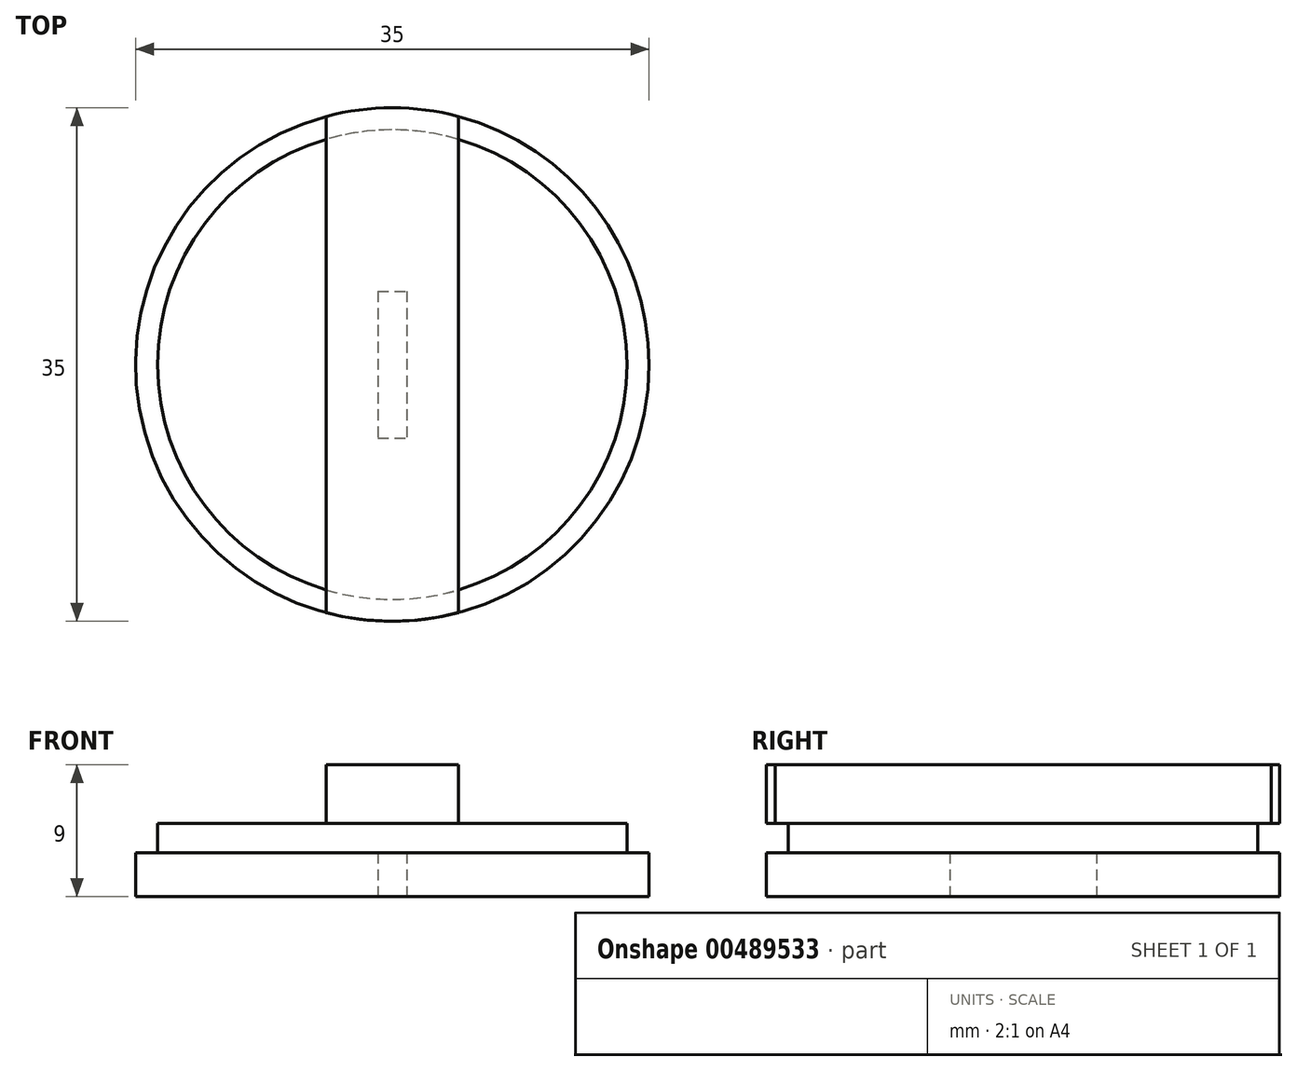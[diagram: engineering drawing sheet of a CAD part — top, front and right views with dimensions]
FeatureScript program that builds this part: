
annotation { "Feature Type Name" : "Feature", "Feature Type Description" : "" }
export const myFeature = defineFeature(function(context is Context, id is Id, definition is map)
    precondition{}
    {
        {
            var Q0;
            Q0=qCreatedBy(makeId("Top.planeOp"),FACE);
            var sketch = newSketch(context, id + "F0", { "sketchPlane" : qUnion([Q0])});
            skCircle(sketch, "E0", {"center": v(0, 0) * mm, "radius": 17.5 * mm});
            skSolve(sketch);
        }
        {
            var Q0;
            Q0 = qSketchRegion(id + "F0", true);
            extrude(context, id + "F1", {"entities" : qUnion([Q0]), "depth" : 3 * mm});
        }
        {
            var Q0;
            Q0=makeQuery(id+"F1.opExtrude","CAP_FACE",FACE,{"disambiguationData":[OSD([sQuery(id+"F0.wireOp",EDGE,"E0")])],"isStart":false});
            var sketch = newSketch(context, id + "F2", { "sketchPlane" : qUnion([Q0])});
            skCircle(sketch, "E1", {"center": v(0, 0) * mm, "radius": 16 * mm});
            skSolve(sketch);
        }
        {
            var Q0;
            Q0 = qSketchRegion(id + "F2", true);
            extrude(context, id + "F3", {"entities" : qUnion([Q0]), "operationType" : NewBodyOperationType.ADD, "depth" : 2 * mm});
        }
        {
            var Q0;
            Q0=makeQuery(id+"F3.opExtrude","CAP_FACE",FACE,{"disambiguationData":[OSD([sQuery(id+"F2.wireOp",EDGE,"E1")])],"isStart":false});
            var sketch = newSketch(context, id + "F4", { "sketchPlane" : qUnion([Q0])});
            skLineSegment(sketch, "E2.left", {"start": v(4.5, 16.91) * mm, "end": v(4.5, -16.91) * mm});
            skLineSegment(sketch, "E2.right", {"start": v(-4.5, 16.91) * mm, "end": v(-4.5, -16.91) * mm});
            skPoint(sketch, "E2.middle", {"position": v(0, 0) * mm});
            skArc(sketch, "E3", {"start": v(4.5, 16.91) * mm, "mid": v(0, 17.5) * mm, "end": v(-4.5, 16.91) * mm});
            skPoint(sketch, "E2.top.end.orphan", {"position": v(-4.5, -30) * mm});
            skPoint(sketch, "E4.orphan", {"position": v(4.5, -30) * mm});
            skArc(sketch, "E5.trimOffspring", {"start": v(-4.5, -16.91) * mm, "mid": v(0, -17.5) * mm, "end": v(4.5, -16.91) * mm});
            skPoint(sketch, "E2.bottom.end.orphan", {"position": v(-4.5, 30) * mm});
            skPoint(sketch, "E6.orphan", {"position": v(4.5, 30) * mm});
            skSolve(sketch);
        }
        {
            var Q0;
            Q0 = qSketchRegion(id + "F4", true);
            extrude(context, id + "F5", {"entities" : qUnion([Q0]), "operationType" : NewBodyOperationType.ADD, "depth" : 4 * mm});
        }
        {
            var Q0;
            Q0=makeQuery(id+"F1.opExtrude","CAP_FACE",FACE,{"disambiguationData":[OSD([sQuery(id+"F0.wireOp",EDGE,"E0")])],"isStart":true});
            var sketch = newSketch(context, id + "F6", { "sketchPlane" : qUnion([Q0])});
            skLineSegment(sketch, "E7.bottom", {"start": v(-1, -5) * mm, "end": v(1, -5) * mm});
            skLineSegment(sketch, "E7.top", {"start": v(-1, 5) * mm, "end": v(1, 5) * mm});
            skLineSegment(sketch, "E7.left", {"start": v(-1, -5) * mm, "end": v(-1, 5) * mm});
            skLineSegment(sketch, "E7.right", {"start": v(1, -5) * mm, "end": v(1, 5) * mm});
            skPoint(sketch, "E7.middle", {"position": v(0, 0) * mm});
            skSolve(sketch);
        }
        {
            var Q0;
            Q0=makeQuery(id+"F6.imprint","IMPRINT",FACE,{"disambiguationData":[TD([[makeQuery(id+"F6.imprint","IMPRINT",EDGE,{"derivedFrom":sQuery(id+"F6.wireOp",EDGE,"E7.bottom")}),1.0]])]});
            extrude(context, id + "F7", {"entities" : qUnion([Q0]), "operationType" : NewBodyOperationType.REMOVE, "oppositeDirection" : true, "depth" : 3 * mm});
        }
    });
